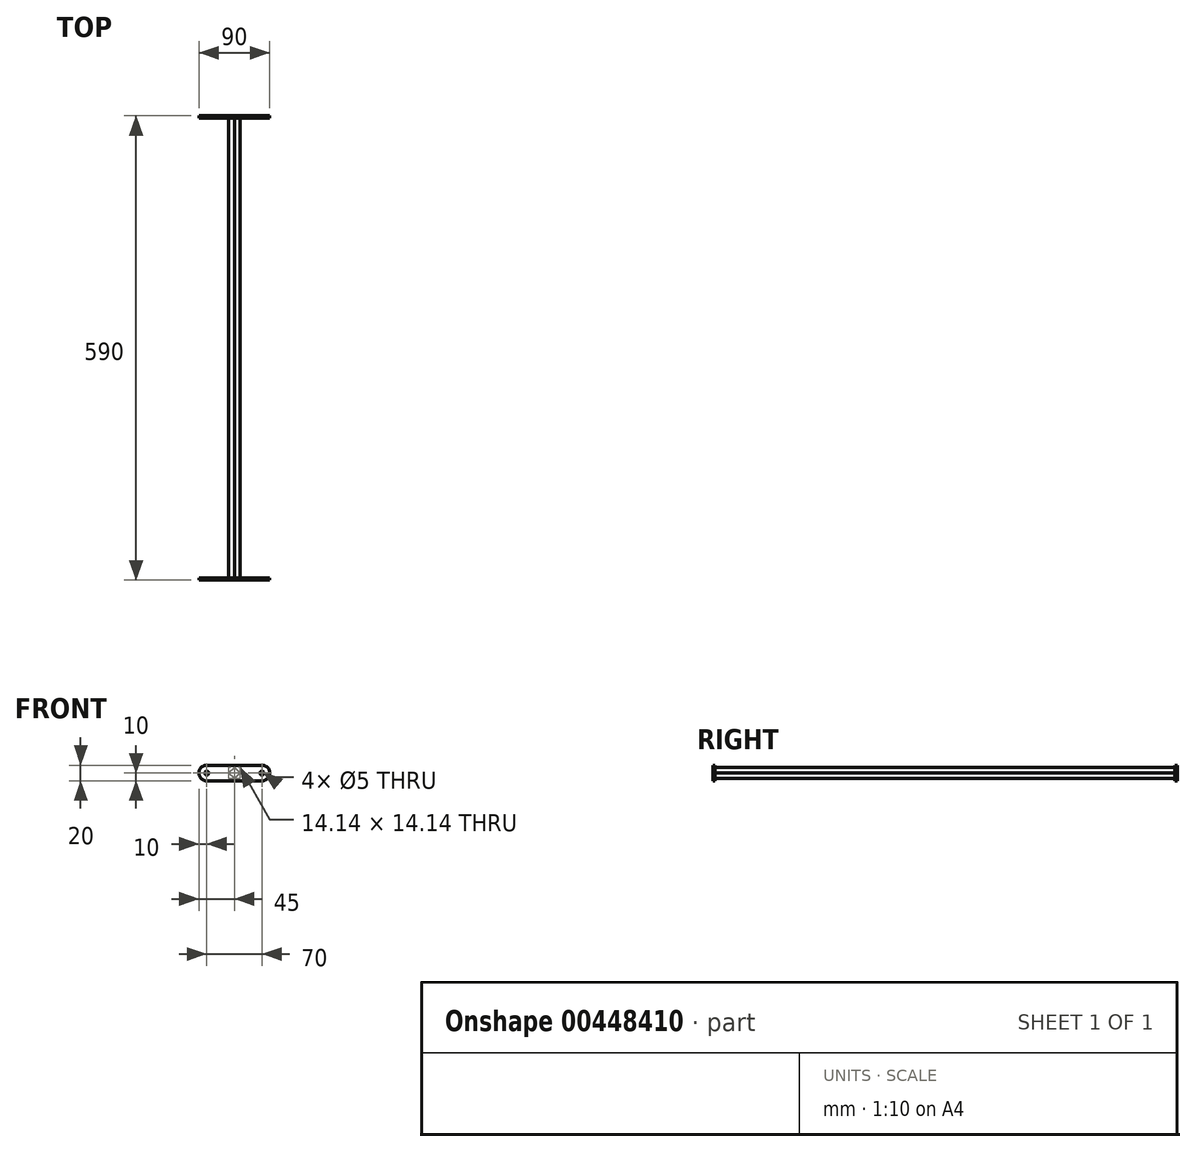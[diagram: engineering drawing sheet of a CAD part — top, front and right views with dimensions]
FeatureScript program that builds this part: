
annotation { "Feature Type Name" : "Feature", "Feature Type Description" : "" }
export const myFeature = defineFeature(function(context is Context, id is Id, definition is map)
    precondition{}
    {
        {
            var Q0;
            Q0=qCreatedBy(makeId("Front.planeOp"),FACE);
            cPlane(context, id + "F0", {"entities" : qUnion([Q0]), "cplaneType" : CPlaneType.OFFSET, "offset" : 292 * mm, "oppositeDirection" : true, "width" : 150 * mm, "height" : 150 * mm});
        }
        {
            var Q0;
            Q0=qCreatedBy(makeId("Front.planeOp"),FACE);
            var sketch = newSketch(context, id + "F1", { "sketchPlane" : qUnion([Q0])});
            skLineSegment(sketch, "E0", {"start": v(0, 0) * mm, "end": v(35, 0) * mm, "construction": true});
            skCircle(sketch, "E1", {"center": v(35, 0) * mm, "radius": 2.5 * mm});
            skLineSegment(sketch, "E2", {"start": v(0, 0) * mm, "end": v(0, 26.9) * mm, "construction": true});
            skArc(sketch, "E3", {"start": v(35, 10) * mm, "mid": v(45, 0) * mm, "end": v(35, -10) * mm});
            skLineSegment(sketch, "E4", {"start": v(35, 10) * mm, "end": v(0, 10) * mm});
            skLineSegment(sketch, "E5", {"start": v(35, -10) * mm, "end": v(0, -10) * mm});
            skLineSegment(sketch, "E6.MirrorCS", {"start": v(0, 0) * mm, "end": v(-35, 0) * mm, "construction": true});
            skCircle(sketch, "E7.MirrorC", {"center": v(-35, 0) * mm, "radius": 2.5 * mm});
            skArc(sketch, "E8.MirrorCS", {"start": v(-35, 10) * mm, "mid": v(-45, 0) * mm, "end": v(-35, -10) * mm});
            skLineSegment(sketch, "E9.MirrorCS", {"start": v(-35, 10) * mm, "end": v(0, 10) * mm});
            skLineSegment(sketch, "E10.MirrorCS", {"start": v(-35, -10) * mm, "end": v(0, -10) * mm});
            skSolve(sketch);
        }
        {
            var Q0;
            Q0 = qSketchRegion(id + "F1", true);
            extrude(context, id + "F2", {"entities" : qUnion([Q0]), "depth" : 3 * mm});
        }
        {
            var Q0;
            Q0=makeQuery(id+"F2.opExtrude","CAP_FACE",FACE,{"disambiguationData":[OSD([sQuery(id+"F1.wireOp",EDGE,"E1"),sQuery(id+"F1.wireOp",EDGE,"E3"),sQuery(id+"F1.wireOp",EDGE,"E4"),sQuery(id+"F1.wireOp",EDGE,"E5"),sQuery(id+"F1.wireOp",EDGE,"E7.MirrorC"),sQuery(id+"F1.wireOp",EDGE,"E8.MirrorCS"),sQuery(id+"F1.wireOp",EDGE,"E9.MirrorCS"),sQuery(id+"F1.wireOp",EDGE,"E10.MirrorCS")])],"isStart":true});
            var sketch = newSketch(context, id + "F3", { "sketchPlane" : qUnion([Q0])});
            skCircle(sketch, "E11.cCircle", {"center": v(0, 0) * mm, "radius": 5 * mm, "construction": true});
            skLineSegment(sketch, "E11.0", {"start": v(0, 7.07) * mm, "end": v(7.07, 0) * mm});
            skLineSegment(sketch, "E11.1", {"start": v(7.07, 0) * mm, "end": v(0, -7.07) * mm});
            skLineSegment(sketch, "E11.2", {"start": v(0, -7.07) * mm, "end": v(-7.07, 0) * mm});
            skLineSegment(sketch, "E11.3", {"start": v(-7.07, 0) * mm, "end": v(0, 7.07) * mm});
            skPoint(sketch, "E11.0.midPoint", {"position": v(3.54, 3.54) * mm});
            skSolve(sketch);
        }
        {
            var Q0;
            Q0=makeQuery(id+"F3.imprint","IMPRINT",FACE,{"disambiguationData":[TD([[makeQuery(id+"F3.imprint","IMPRINT",EDGE,{"derivedFrom":sQuery(id+"F3.wireOp",EDGE,"E11.0")}),-1.0]])]});
            var Q1;
            Q1=qCreatedBy(id+"F0.planeOp",FACE);
            extrude(context, id + "F4", {"entities" : qUnion([Q0]), "operationType" : NewBodyOperationType.ADD, "endBound" : BoundingType.UP_TO_SURFACE, "endBoundEntityFace" : qUnion([Q1]), "depth" : 197 * mm});
        }
        {
            var Q0;
            Q0=makeQuery(id+"F2.opExtrude","SWEPT_BODY",BODY,{"disambiguationData":[OSD([sQuery(id+"F1.wireOp",EDGE,"E1"),sQuery(id+"F1.wireOp",EDGE,"E3"),sQuery(id+"F1.wireOp",EDGE,"E4"),sQuery(id+"F1.wireOp",EDGE,"E5"),sQuery(id+"F1.wireOp",EDGE,"E7.MirrorC"),sQuery(id+"F1.wireOp",EDGE,"E8.MirrorCS"),sQuery(id+"F1.wireOp",EDGE,"E9.MirrorCS"),sQuery(id+"F1.wireOp",EDGE,"E10.MirrorCS")])]});
            var Q1;
            Q1=qCreatedBy(id+"F0.planeOp",FACE);
            mirror(context, id + "F5", {"operationType" : NewBodyOperationType.ADD, "entities" : qUnion([Q0]), "mirrorPlane" : qUnion([Q1])});
        }
    });
